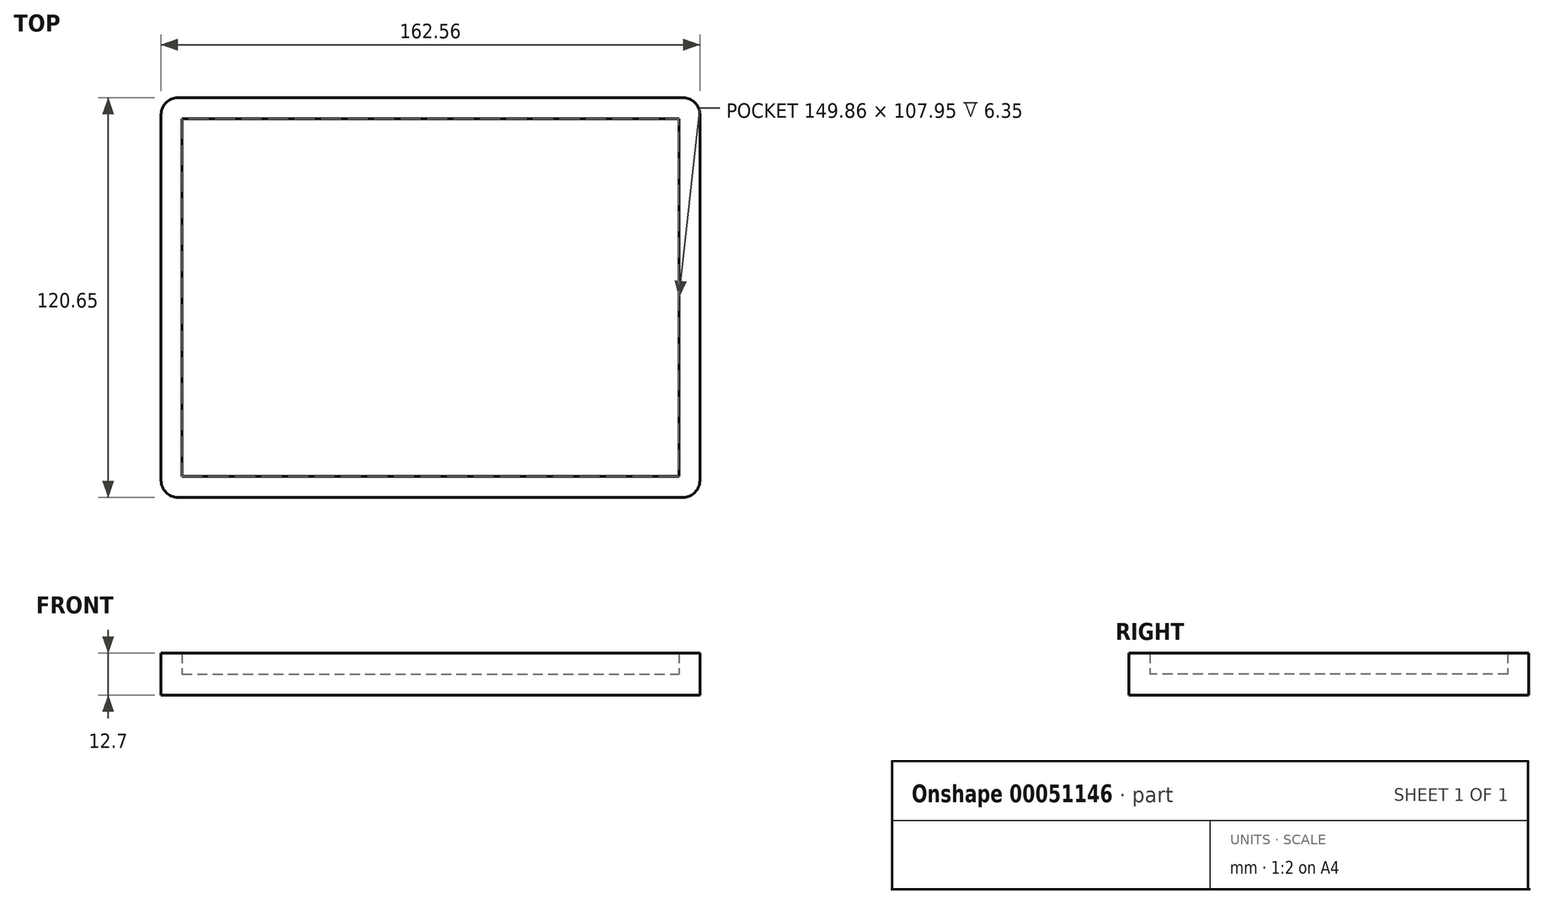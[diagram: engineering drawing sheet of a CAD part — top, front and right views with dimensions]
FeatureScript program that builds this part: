
annotation { "Feature Type Name" : "Feature", "Feature Type Description" : "" }
export const myFeature = defineFeature(function(context is Context, id is Id, definition is map)
    precondition{}
    {
        {
            var Q0;
            Q0=qCreatedBy(makeId("Top.planeOp"),FACE);
            var sketch = newSketch(context, id + "F0", { "sketchPlane" : qUnion([Q0])});
            skLineSegment(sketch, "E0.top", {"start": v(-63.69, 52.35) * mm, "end": v(98.87, 52.35) * mm});
            skLineSegment(sketch, "E1", {"start": v(-63.69, 52.35) * mm, "end": v(-63.69, -68.3) * mm});
            skLineSegment(sketch, "E2", {"start": v(98.87, 52.35) * mm, "end": v(98.87, -68.3) * mm});
            skLineSegment(sketch, "E3", {"start": v(-63.69, -68.3) * mm, "end": v(98.87, -68.3) * mm});
            skSolve(sketch);
        }
        {
            var Q0;
            Q0 = qSketchRegion(id + "F0", true);
            extrude(context, id + "F1", {"entities" : qUnion([Q0]), "depth" : 6.35 * mm});
        }
        {
            var Q0;
            Q0=makeQuery(id+"F1.opExtrude","CAP_FACE",FACE,{"disambiguationData":[OSD([sQuery(id+"F0.wireOp",EDGE,"E0.top"),sQuery(id+"F0.wireOp",EDGE,"E1"),sQuery(id+"F0.wireOp",EDGE,"E2"),sQuery(id+"F0.wireOp",EDGE,"E3")])],"isStart":false});
            var sketch = newSketch(context, id + "F2", { "sketchPlane" : qUnion([Q0])});
            skLineSegment(sketch, "E4.bottom", {"start": v(-63.69, 52.35) * mm, "end": v(98.87, 52.35) * mm});
            skLineSegment(sketch, "E4.top", {"start": v(-63.69, -68.3) * mm, "end": v(98.87, -68.3) * mm});
            skLineSegment(sketch, "E4.left", {"start": v(-63.69, 52.35) * mm, "end": v(-63.69, -68.3) * mm});
            skLineSegment(sketch, "E4.right", {"start": v(98.87, 52.35) * mm, "end": v(98.87, -68.3) * mm});
            skLineSegment(sketch, "E5.bottom", {"start": v(-57.34, 46) * mm, "end": v(92.52, 46) * mm});
            skLineSegment(sketch, "E5.top", {"start": v(-57.34, -61.95) * mm, "end": v(92.52, -61.95) * mm});
            skLineSegment(sketch, "E5.left", {"start": v(-57.34, 46) * mm, "end": v(-57.34, -61.95) * mm});
            skLineSegment(sketch, "E5.right", {"start": v(92.52, 46) * mm, "end": v(92.52, -61.95) * mm});
            skSolve(sketch);
        }
        {
            var Q0;
            Q0 = qSketchRegion(id + "F2", true);
            extrude(context, id + "F3", {"entities" : qUnion([Q0]), "operationType" : NewBodyOperationType.ADD, "depth" : 6.35 * mm});
        }
        {
            var Q0;
            Q0=makeQuery(id+"F3.boolean.opBoolean","MERGE",EDGE,{"derivedFrom":[makeQuery(id+"F1.opExtrude","SWEPT_EDGE",EDGE,{"disambiguationData":[OSD([sQuery(id+"F0.wireOp",EDGE,"E2"),sQuery(id+"F0.wireOp",EDGE,"E3")])]}),makeQuery(id+"F3.opExtrude","SWEPT_EDGE",EDGE,{"disambiguationData":[OSD([sQuery(id+"F2.wireOp",EDGE,"E4.top"),sQuery(id+"F2.wireOp",EDGE,"E4.right")])]})]});
            var Q1;
            Q1=makeQuery(id+"F3.boolean.opBoolean","MERGE",EDGE,{"derivedFrom":[makeQuery(id+"F1.opExtrude","SWEPT_EDGE",EDGE,{"disambiguationData":[OSD([sQuery(id+"F0.wireOp",EDGE,"E0.top"),sQuery(id+"F0.wireOp",EDGE,"E2")])]}),makeQuery(id+"F3.opExtrude","SWEPT_EDGE",EDGE,{"disambiguationData":[OSD([sQuery(id+"F2.wireOp",EDGE,"E4.bottom"),sQuery(id+"F2.wireOp",EDGE,"E4.right")])]})]});
            var Q2;
            Q2=makeQuery(id+"F3.boolean.opBoolean","MERGE",EDGE,{"derivedFrom":[makeQuery(id+"F1.opExtrude","SWEPT_EDGE",EDGE,{"disambiguationData":[OSD([sQuery(id+"F0.wireOp",EDGE,"E0.top"),sQuery(id+"F0.wireOp",EDGE,"E1")])]}),makeQuery(id+"F3.opExtrude","SWEPT_EDGE",EDGE,{"disambiguationData":[OSD([sQuery(id+"F2.wireOp",EDGE,"E4.bottom"),sQuery(id+"F2.wireOp",EDGE,"E4.left")])]})]});
            var Q3;
            Q3=makeQuery(id+"F3.boolean.opBoolean","MERGE",EDGE,{"derivedFrom":[makeQuery(id+"F1.opExtrude","SWEPT_EDGE",EDGE,{"disambiguationData":[OSD([sQuery(id+"F0.wireOp",EDGE,"E1"),sQuery(id+"F0.wireOp",EDGE,"E3")])]}),makeQuery(id+"F3.opExtrude","SWEPT_EDGE",EDGE,{"disambiguationData":[OSD([sQuery(id+"F2.wireOp",EDGE,"E4.top"),sQuery(id+"F2.wireOp",EDGE,"E4.left")])]})]});
            fillet(context, id + "F4", {"entities" : qUnion([Q0, Q1, Q2, Q3]), "radius" : 5.08 * mm, "tangentPropagation" : true, "allowEdgeOverflow" : false});
        }
    });
